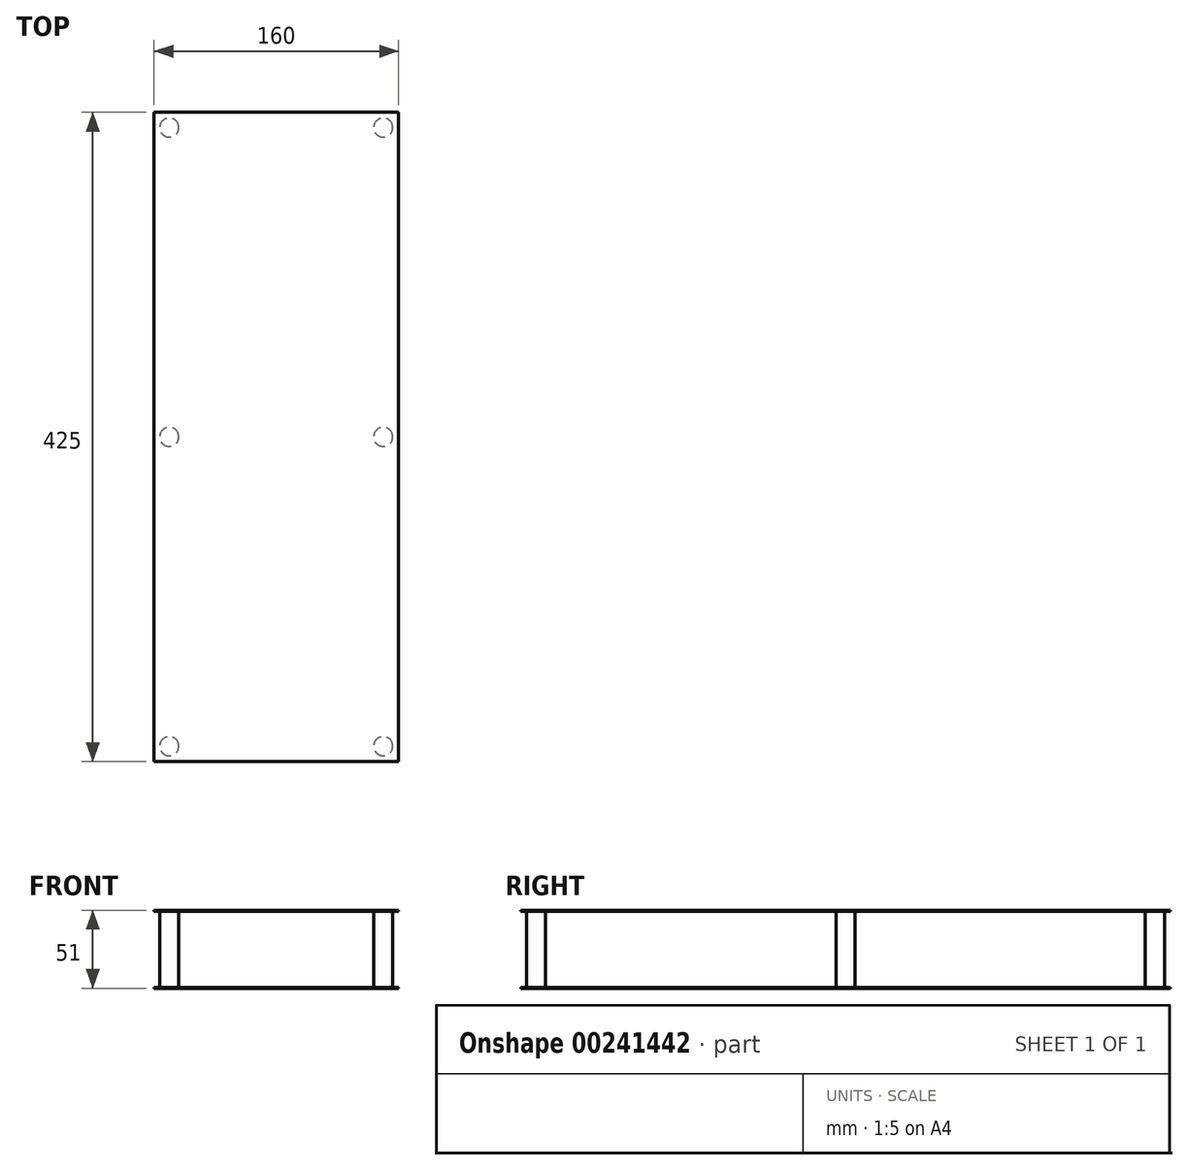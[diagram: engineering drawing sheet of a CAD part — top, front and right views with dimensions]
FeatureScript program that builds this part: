
annotation { "Feature Type Name" : "Feature", "Feature Type Description" : "" }
export const myFeature = defineFeature(function(context is Context, id is Id, definition is map)
    precondition{}
    {
        {
            var Q0;
            Q0=qCreatedBy(makeId("Top.planeOp"),FACE);
            var sketch = newSketch(context, id + "F0", { "sketchPlane" : qUnion([Q0])});
            skLineSegment(sketch, "E0.bottom", {"start": v(-80, 212.5) * mm, "end": v(80, 212.5) * mm});
            skLineSegment(sketch, "E0.top", {"start": v(-80, -212.5) * mm, "end": v(80, -212.5) * mm});
            skLineSegment(sketch, "E0.left", {"start": v(-80, 212.5) * mm, "end": v(-80, -212.5) * mm});
            skLineSegment(sketch, "E0.right", {"start": v(80, 212.5) * mm, "end": v(80, -212.5) * mm});
            skPoint(sketch, "E0.middle", {"position": v(0, 0) * mm});
            skSolve(sketch);
        }
        {
            var Q0;
            Q0 = qSketchRegion(id + "F0", true);
            extrude(context, id + "F1", {"entities" : qUnion([Q0]), "oppositeDirection" : true, "depth" : .5 * mm});
        }
        {
            var Q0;
            Q0=makeQuery(id+"F0.imprint","IMPRINT",FACE,{"disambiguationData":[TD([[makeQuery(id+"F0.imprint","IMPRINT",EDGE,{"derivedFrom":sQuery(id+"F0.wireOp",EDGE,"E0.bottom")}),-1.0]])]});
            var sketch = newSketch(context, id + "F2", { "sketchPlane" : qUnion([Q0])});
            skCircle(sketch, "E1", {"center": v(-70, 202.5) * mm, "radius": 6.25 * mm});
            skCircle(sketch, "E2.0.1.0", {"center": v(-70, 0) * mm, "radius": 6.25 * mm});
            skCircle(sketch, "E2.0.2.0", {"center": v(-70, -202.5) * mm, "radius": 6.25 * mm});
            skCircle(sketch, "E2.1.0.0", {"center": v(70, 202.5) * mm, "radius": 6.25 * mm});
            skCircle(sketch, "E2.1.1.0", {"center": v(70, 0) * mm, "radius": 6.25 * mm});
            skCircle(sketch, "E2.1.2.0", {"center": v(70, -202.5) * mm, "radius": 6.25 * mm});
            skLineSegment(sketch, "E2.direction1", {"start": v(-70, 202.5) * mm, "end": v(70, 202.5) * mm, "construction": true});
            skLineSegment(sketch, "E2.direction2", {"start": v(-70, 202.5) * mm, "end": v(-70, 0) * mm, "construction": true});
            skSolve(sketch);
        }
        {
            var Q0;
            Q0 = qSketchRegion(id + "F2", true);
            extrude(context, id + "F3", {"entities" : qUnion([Q0]), "operationType" : NewBodyOperationType.ADD, "depth" : 50 * mm});
        }
        {
            var Q0;
            Q0=makeQuery(id+"F3.opExtrude","CAP_FACE",FACE,{"disambiguationData":[OSD([sQuery(id+"F2.wireOp",EDGE,"E1")])],"isStart":false});
            var sketch = newSketch(context, id + "F4", { "sketchPlane" : qUnion([Q0])});
            skLineSegment(sketch, "E3.bottom", {"start": v(-80, 212.5) * mm, "end": v(80, 212.5) * mm});
            skLineSegment(sketch, "E3.top", {"start": v(-80, -212.5) * mm, "end": v(80, -212.5) * mm});
            skLineSegment(sketch, "E3.left", {"start": v(-80, 212.5) * mm, "end": v(-80, -212.5) * mm});
            skLineSegment(sketch, "E3.right", {"start": v(80, 212.5) * mm, "end": v(80, -212.5) * mm});
            skPoint(sketch, "E3.middle", {"position": v(0, 0) * mm});
            skSolve(sketch);
        }
        {
            var Q0;
            Q0 = qSketchRegion(id + "F4", true);
            extrude(context, id + "F5", {"entities" : qUnion([Q0]), "operationType" : NewBodyOperationType.ADD, "depth" : .5 * mm});
        }
    });
